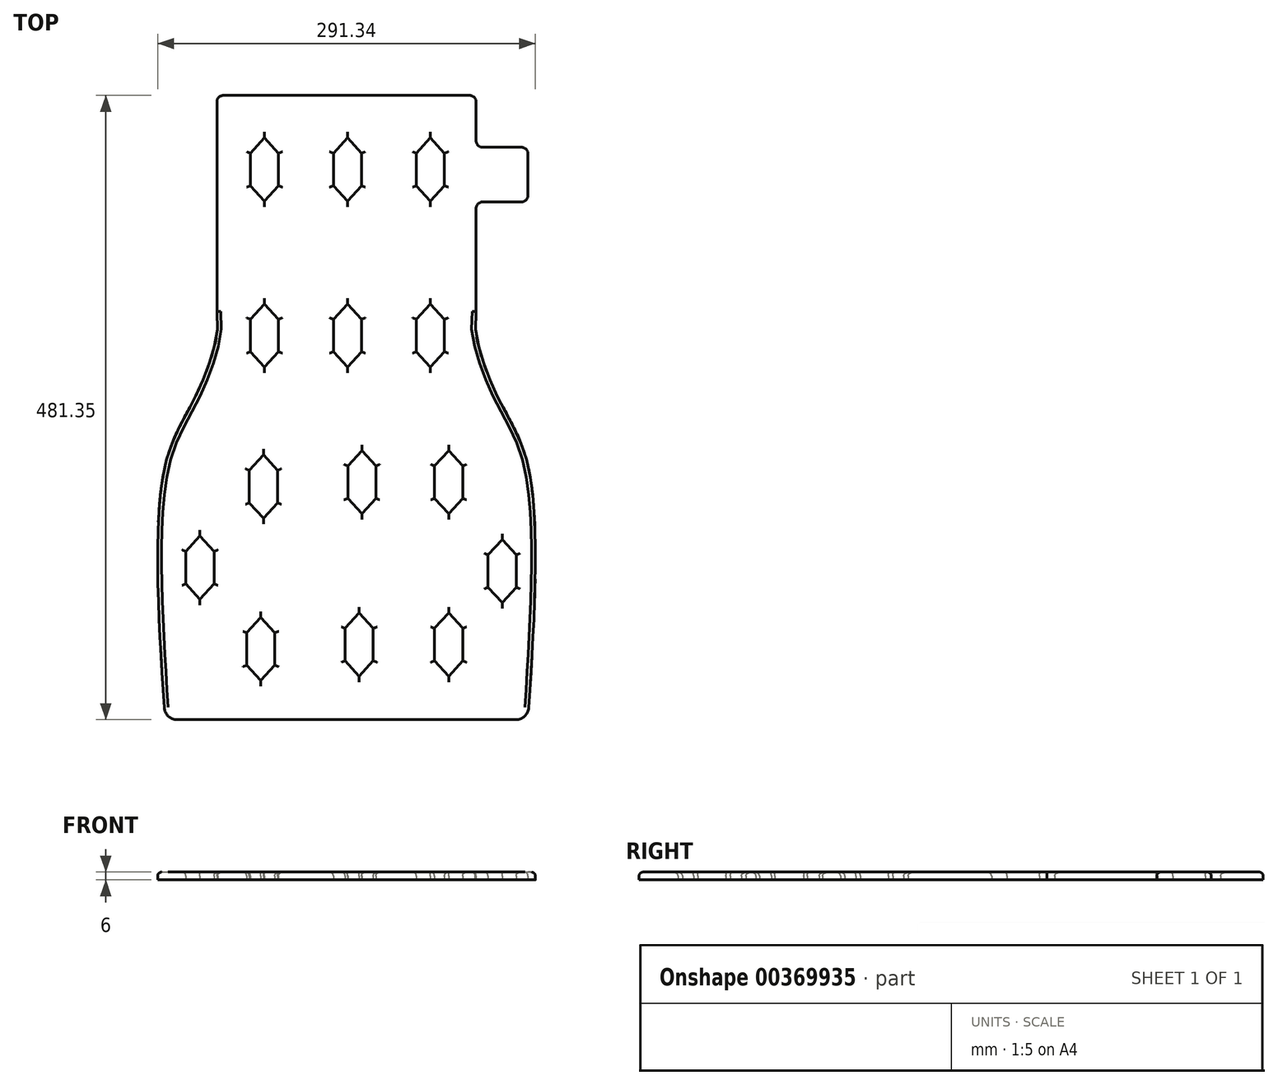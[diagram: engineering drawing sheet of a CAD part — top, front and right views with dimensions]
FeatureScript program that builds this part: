
annotation { "Feature Type Name" : "Feature", "Feature Type Description" : "" }
export const myFeature = defineFeature(function(context is Context, id is Id, definition is map)
    precondition{}
    {
        {
            var Q0;
            Q0=qCreatedBy(makeId("Top.planeOp"),FACE);
            var sketch = newSketch(context, id + "F0", { "sketchPlane" : qUnion([Q0])});
            skLineSegment(sketch, "E0", {"start": v(0, 262.18) * mm, "end": v(95, 262.18) * mm});
            skLineSegment(sketch, "E1", {"start": v(0, 262.18) * mm, "end": v(-95, 262.18) * mm});
            skLineSegment(sketch, "E2", {"start": v(130.62, -219.17) * mm, "end": v(-130.62, -219.17) * mm});
            skFitSpline(sketch, "E3", {"points": [v(-140, -219.17) * mm, v(-140, -23.78) * mm, v(-116.25, 30.48) * mm, v(-100, 77.75) * mm, v(-100, 95.38) * mm], "startDerivative": vector(-34.72, 539.25) * mm, "endDerivative": vector(-13.07, 120.29) * mm});
            skFitSpline(sketch, "E4.MirrorCS", {"points": [v(140, -219.17) * mm, v(140, -23.78) * mm, v(116.25, 30.48) * mm, v(100, 77.75) * mm, v(100, 95.38) * mm], "startDerivative": vector(34.72, 539.25) * mm, "endDerivative": vector(13.07, 120.29) * mm});
            skLineSegment(sketch, "E5", {"start": v(-100, 257.18) * mm, "end": v(-100, 95.38) * mm});
            skLineSegment(sketch, "E6", {"start": v(100, 95.38) * mm, "end": v(100, 175.09) * mm});
            skPoint(sketch, "E7.visualSharp", {"position": v(-100, 262.18) * mm});
            skArc(sketch, "E7.filletArc", {"start": v(-95, 262.18) * mm, "mid": v(-98.54, 260.72) * mm, "end": v(-100, 257.18) * mm});
            skPoint(sketch, "E8.visualSharp", {"position": v(100, 262.18) * mm});
            skArc(sketch, "E8.filletArc", {"start": v(100, 257.18) * mm, "mid": v(98.54, 260.72) * mm, "end": v(95, 262.18) * mm});
            skLineSegment(sketch, "E9", {"start": v(100, 262.18) * mm, "end": v(100, 227.18) * mm});
            skLineSegment(sketch, "E10", {"start": v(105, 222.18) * mm, "end": v(135, 222.18) * mm});
            skLineSegment(sketch, "E11", {"start": v(140, 217.18) * mm, "end": v(140, 185.09) * mm});
            skLineSegment(sketch, "E12", {"start": v(135, 180.09) * mm, "end": v(105, 180.09) * mm});
            skArc(sketch, "E13.filletArc", {"start": v(105, 180.09) * mm, "mid": v(101.46, 178.62) * mm, "end": v(100, 175.09) * mm});
            skPoint(sketch, "E14.visualSharp", {"position": v(140, 180.09) * mm});
            skArc(sketch, "E14.filletArc", {"start": v(135, 180.09) * mm, "mid": v(138.54, 181.55) * mm, "end": v(140, 185.09) * mm});
            skPoint(sketch, "E15.visualSharp", {"position": v(140, 222.18) * mm});
            skArc(sketch, "E15.filletArc", {"start": v(140, 217.18) * mm, "mid": v(138.54, 220.72) * mm, "end": v(135, 222.18) * mm});
            skPoint(sketch, "E16.visualSharp", {"position": v(100, 222.18) * mm});
            skArc(sketch, "E16.filletArc", {"start": v(100, 227.18) * mm, "mid": v(101.46, 223.65) * mm, "end": v(105, 222.18) * mm});
            skArc(sketch, "E17.filletArc", {"start": v(130.62, -219.17) * mm, "mid": v(137.46, -216.46) * mm, "end": v(140.6, -209.8) * mm});
            skArc(sketch, "E18.filletArc", {"start": v(-140.6, -209.8) * mm, "mid": v(-137.46, -216.46) * mm, "end": v(-130.62, -219.17) * mm});
            skLineSegment(sketch, "E19.left", {"start": v(-52.46, 217.58) * mm, "end": v(-52.46, 192.58) * mm});
            skLineSegment(sketch, "E19.right", {"start": v(-74.1, 217.58) * mm, "end": v(-74.1, 192.58) * mm});
            skPoint(sketch, "E20.endSnap0", {"position": v(-63.28, 136.49) * mm});
            skLineSegment(sketch, "E21", {"start": v(-63.28, 180.7) * mm, "end": v(-52.46, 192.58) * mm});
            skPoint(sketch, "E22.endSnap0", {"position": v(46.38, 56.52) * mm});
            skLineSegment(sketch, "E23.MirrorCS", {"start": v(-63.28, 229.44) * mm, "end": v(-52.46, 217.58) * mm});
            skLineSegment(sketch, "E24.MirrorCS", {"start": v(-74.1, 217.58) * mm, "end": v(-63.28, 229.44) * mm});
            skLineSegment(sketch, "E25.0.1.0", {"start": v(-74.1, 89.58) * mm, "end": v(-63.28, 101.44) * mm});
            skLineSegment(sketch, "E25.0.1.1", {"start": v(-74.1, 89.58) * mm, "end": v(-74.1, 64.58) * mm});
            skLineSegment(sketch, "E25.0.1.2", {"start": v(-74.1, 64.58) * mm, "end": v(-63.28, 52.7) * mm});
            skLineSegment(sketch, "E25.0.1.3", {"start": v(-63.28, 52.7) * mm, "end": v(-52.46, 64.58) * mm});
            skLineSegment(sketch, "E25.0.1.4", {"start": v(-52.46, 89.58) * mm, "end": v(-52.46, 64.58) * mm});
            skLineSegment(sketch, "E25.0.1.5", {"start": v(-63.28, 101.44) * mm, "end": v(-52.46, 89.58) * mm});
            skLineSegment(sketch, "E25.1.0.0", {"start": v(-10.1, 217.58) * mm, "end": v(0.72, 229.44) * mm});
            skLineSegment(sketch, "E25.1.0.1", {"start": v(-10.1, 217.58) * mm, "end": v(-10.1, 192.58) * mm});
            skLineSegment(sketch, "E25.1.0.2", {"start": v(-10.1, 192.58) * mm, "end": v(0.72, 180.7) * mm});
            skLineSegment(sketch, "E25.1.0.3", {"start": v(0.72, 180.7) * mm, "end": v(11.54, 192.58) * mm});
            skLineSegment(sketch, "E25.1.0.4", {"start": v(11.54, 217.58) * mm, "end": v(11.54, 192.58) * mm});
            skLineSegment(sketch, "E25.1.0.5", {"start": v(0.72, 229.44) * mm, "end": v(11.54, 217.58) * mm});
            skLineSegment(sketch, "E25.1.1.0", {"start": v(-10.1, 89.58) * mm, "end": v(0.72, 101.44) * mm});
            skLineSegment(sketch, "E25.1.1.1", {"start": v(-10.1, 89.58) * mm, "end": v(-10.1, 64.58) * mm});
            skLineSegment(sketch, "E25.1.1.2", {"start": v(-10.1, 64.58) * mm, "end": v(0.72, 52.7) * mm});
            skLineSegment(sketch, "E25.1.1.3", {"start": v(0.72, 52.7) * mm, "end": v(11.54, 64.58) * mm});
            skLineSegment(sketch, "E25.1.1.4", {"start": v(11.54, 89.58) * mm, "end": v(11.54, 64.58) * mm});
            skLineSegment(sketch, "E25.1.1.5", {"start": v(0.72, 101.44) * mm, "end": v(11.54, 89.58) * mm});
            skLineSegment(sketch, "E25.2.0.0", {"start": v(53.9, 217.58) * mm, "end": v(64.72, 229.44) * mm});
            skLineSegment(sketch, "E25.2.0.1", {"start": v(53.9, 217.58) * mm, "end": v(53.9, 192.58) * mm});
            skLineSegment(sketch, "E25.2.0.2", {"start": v(53.9, 192.58) * mm, "end": v(64.72, 180.7) * mm});
            skLineSegment(sketch, "E25.2.0.3", {"start": v(64.72, 180.7) * mm, "end": v(75.54, 192.58) * mm});
            skLineSegment(sketch, "E25.2.0.4", {"start": v(75.54, 217.58) * mm, "end": v(75.54, 192.58) * mm});
            skLineSegment(sketch, "E25.2.0.5", {"start": v(64.72, 229.44) * mm, "end": v(75.54, 217.58) * mm});
            skLineSegment(sketch, "E25.2.1.0", {"start": v(53.9, 89.58) * mm, "end": v(64.72, 101.44) * mm});
            skLineSegment(sketch, "E25.2.1.1", {"start": v(53.9, 89.58) * mm, "end": v(53.9, 64.58) * mm});
            skLineSegment(sketch, "E25.2.1.2", {"start": v(53.9, 64.58) * mm, "end": v(64.72, 52.7) * mm});
            skLineSegment(sketch, "E25.2.1.3", {"start": v(64.72, 52.7) * mm, "end": v(75.54, 64.58) * mm});
            skLineSegment(sketch, "E25.2.1.4", {"start": v(75.54, 89.58) * mm, "end": v(75.54, 64.58) * mm});
            skLineSegment(sketch, "E25.2.1.5", {"start": v(64.72, 101.44) * mm, "end": v(75.54, 89.58) * mm});
            skLineSegment(sketch, "E25.direction1", {"start": v(-63.28, 180.7) * mm, "end": v(0.72, 180.7) * mm, "construction": true});
            skLineSegment(sketch, "E25.direction2", {"start": v(-63.28, 180.7) * mm, "end": v(-63.28, 52.7) * mm, "construction": true});
            skLineSegment(sketch, "E26.left", {"start": v(-53.3, -26.91) * mm, "end": v(-53.3, -51.91) * mm});
            skLineSegment(sketch, "E26.right", {"start": v(-74.93, -26.91) * mm, "end": v(-74.93, -51.91) * mm});
            skLineSegment(sketch, "E27", {"start": v(-74.93, -51.91) * mm, "end": v(-64.11, -63.78) * mm});
            skLineSegment(sketch, "E28", {"start": v(-64.11, -63.78) * mm, "end": v(-53.3, -51.91) * mm});
            skLineSegment(sketch, "E29.MirrorCS", {"start": v(-64.11, -15.05) * mm, "end": v(-53.3, -26.91) * mm});
            skLineSegment(sketch, "E30.MirrorCS", {"start": v(-74.93, -26.91) * mm, "end": v(-64.11, -15.05) * mm});
            skLineSegment(sketch, "E31.0.1.0", {"start": v(-76.97, -152.13) * mm, "end": v(-66.16, -140.27) * mm});
            skLineSegment(sketch, "E31.0.1.1", {"start": v(-66.16, -140.27) * mm, "end": v(-55.34, -152.13) * mm});
            skLineSegment(sketch, "E31.0.1.2", {"start": v(-55.34, -152.13) * mm, "end": v(-55.34, -177.13) * mm});
            skLineSegment(sketch, "E31.0.1.3", {"start": v(-66.16, -189) * mm, "end": v(-55.34, -177.13) * mm});
            skLineSegment(sketch, "E31.0.1.4", {"start": v(-76.97, -177.13) * mm, "end": v(-66.16, -189) * mm});
            skLineSegment(sketch, "E31.0.1.5", {"start": v(-76.97, -152.13) * mm, "end": v(-76.97, -177.13) * mm});
            skLineSegment(sketch, "E31.1.0.0", {"start": v(1.03, -23.5) * mm, "end": v(11.84, -11.63) * mm});
            skLineSegment(sketch, "E31.1.0.1", {"start": v(11.84, -11.63) * mm, "end": v(22.66, -23.5) * mm});
            skLineSegment(sketch, "E31.1.0.2", {"start": v(22.66, -23.5) * mm, "end": v(22.66, -48.5) * mm});
            skLineSegment(sketch, "E31.1.0.3", {"start": v(11.84, -60.36) * mm, "end": v(22.66, -48.5) * mm});
            skLineSegment(sketch, "E31.1.0.4", {"start": v(1.03, -48.5) * mm, "end": v(11.84, -60.36) * mm});
            skLineSegment(sketch, "E31.1.0.5", {"start": v(1.03, -23.5) * mm, "end": v(1.03, -48.5) * mm});
            skLineSegment(sketch, "E31.1.1.0", {"start": v(-1.02, -148.72) * mm, "end": v(9.8, -136.85) * mm});
            skLineSegment(sketch, "E31.1.1.1", {"start": v(9.8, -136.85) * mm, "end": v(20.61, -148.72) * mm});
            skLineSegment(sketch, "E31.1.1.2", {"start": v(20.61, -148.72) * mm, "end": v(20.61, -173.72) * mm});
            skLineSegment(sketch, "E31.1.1.3", {"start": v(9.8, -185.58) * mm, "end": v(20.61, -173.72) * mm});
            skLineSegment(sketch, "E31.1.1.4", {"start": v(-1.02, -173.72) * mm, "end": v(9.8, -185.58) * mm});
            skLineSegment(sketch, "E31.1.1.5", {"start": v(-1.02, -148.72) * mm, "end": v(-1.02, -173.72) * mm});
            skLineSegment(sketch, "E31.direction1", {"start": v(-64.11, -63.78) * mm, "end": v(11.84, -60.36) * mm, "construction": true});
            skLineSegment(sketch, "E31.direction2", {"start": v(-64.11, -63.78) * mm, "end": v(-66.16, -189) * mm, "construction": true});
            skLineSegment(sketch, "E32.left", {"start": v(-102.2, -89.43) * mm, "end": v(-102.2, -114.43) * mm});
            skLineSegment(sketch, "E32.right", {"start": v(-123.84, -89.43) * mm, "end": v(-123.84, -114.43) * mm});
            skLineSegment(sketch, "E33", {"start": v(-123.84, -114.43) * mm, "end": v(-113.02, -126.3) * mm});
            skLineSegment(sketch, "E34", {"start": v(-113.02, -126.3) * mm, "end": v(-102.2, -114.43) * mm});
            skLineSegment(sketch, "E35.MirrorCS", {"start": v(-113.02, -77.56) * mm, "end": v(-102.2, -89.43) * mm});
            skLineSegment(sketch, "E36.MirrorCS", {"start": v(-123.84, -89.43) * mm, "end": v(-113.02, -77.56) * mm});
            skLineSegment(sketch, "E37.left", {"start": v(130.86, -92.1) * mm, "end": v(130.86, -117.1) * mm});
            skLineSegment(sketch, "E37.right", {"start": v(109.23, -92.1) * mm, "end": v(109.23, -117.1) * mm});
            skLineSegment(sketch, "E38", {"start": v(109.23, -117.1) * mm, "end": v(120.04, -128.96) * mm});
            skLineSegment(sketch, "E39", {"start": v(120.04, -128.96) * mm, "end": v(130.86, -117.1) * mm});
            skLineSegment(sketch, "E40.MirrorCS", {"start": v(120.04, -80.23) * mm, "end": v(130.86, -92.1) * mm});
            skLineSegment(sketch, "E41.MirrorCS", {"start": v(109.23, -92.1) * mm, "end": v(120.04, -80.23) * mm});
            skLineSegment(sketch, "E42.left", {"start": v(89.58, -23.5) * mm, "end": v(89.58, -48.5) * mm});
            skLineSegment(sketch, "E42.right", {"start": v(67.95, -23.5) * mm, "end": v(67.95, -48.5) * mm});
            skLineSegment(sketch, "E43", {"start": v(67.95, -48.5) * mm, "end": v(78.76, -60.36) * mm});
            skLineSegment(sketch, "E44", {"start": v(78.76, -60.36) * mm, "end": v(89.58, -48.5) * mm});
            skLineSegment(sketch, "E45.MirrorCS", {"start": v(78.76, -11.63) * mm, "end": v(89.58, -23.5) * mm});
            skLineSegment(sketch, "E46.MirrorCS", {"start": v(67.95, -23.5) * mm, "end": v(78.76, -11.63) * mm});
            skLineSegment(sketch, "E47.left", {"start": v(89.58, -148.72) * mm, "end": v(89.58, -173.72) * mm});
            skLineSegment(sketch, "E47.right", {"start": v(67.95, -148.72) * mm, "end": v(67.95, -173.72) * mm});
            skLineSegment(sketch, "E48", {"start": v(67.95, -173.72) * mm, "end": v(78.76, -185.58) * mm});
            skLineSegment(sketch, "E49", {"start": v(78.76, -185.58) * mm, "end": v(89.58, -173.72) * mm});
            skLineSegment(sketch, "E50.MirrorCS", {"start": v(78.76, -136.85) * mm, "end": v(89.58, -148.72) * mm});
            skLineSegment(sketch, "E51.MirrorCS", {"start": v(67.95, -148.72) * mm, "end": v(78.76, -136.85) * mm});
            skLineSegment(sketch, "E52", {"start": v(-74.1, 192.58) * mm, "end": v(-63.28, 180.7) * mm});
            skSolve(sketch);
        }
        {
            var Q0;
            Q0=makeQuery(id+"F0.imprint","IMPRINT",FACE,{"disambiguationData":[TD([[makeQuery(id+"F0.imprint","IMPRINT",EDGE,{"derivedFrom":sQuery(id+"F0.wireOp",EDGE,"E0")}),-1.0]])]});
            extrude(context, id + "F1", {"entities" : qUnion([Q0]), "depth" : 6 * mm, "offsetDistance" : 25 * mm});
        }
        {
            var Q0;
            Q0=makeQuery(id+"F1.opExtrude","CAP_FACE",FACE,{"disambiguationData":[OSD([sQuery(id+"F0.wireOp",EDGE,"E0"),sQuery(id+"F0.wireOp",EDGE,"E1"),sQuery(id+"F0.wireOp",EDGE,"E2"),sQuery(id+"F0.wireOp",EDGE,"E3"),sQuery(id+"F0.wireOp",EDGE,"E4.MirrorCS"),sQuery(id+"F0.wireOp",EDGE,"E5"),sQuery(id+"F0.wireOp",EDGE,"E6"),sQuery(id+"F0.wireOp",EDGE,"E7.filletArc"),sQuery(id+"F0.wireOp",EDGE,"E8.filletArc"),sQuery(id+"F0.wireOp",EDGE,"E9"),sQuery(id+"F0.wireOp",EDGE,"E10"),sQuery(id+"F0.wireOp",EDGE,"E11"),sQuery(id+"F0.wireOp",EDGE,"E12"),sQuery(id+"F0.wireOp",EDGE,"E13.filletArc"),sQuery(id+"F0.wireOp",EDGE,"E14.filletArc"),sQuery(id+"F0.wireOp",EDGE,"E15.filletArc"),sQuery(id+"F0.wireOp",EDGE,"E16.filletArc"),sQuery(id+"F0.wireOp",EDGE,"E17.filletArc"),sQuery(id+"F0.wireOp",EDGE,"E18.filletArc"),sQuery(id+"F0.wireOp",EDGE,"E19.left"),sQuery(id+"F0.wireOp",EDGE,"E19.right"),sQuery(id+"F0.wireOp",EDGE,"E21"),sQuery(id+"F0.wireOp",EDGE,"E23.MirrorCS"),sQuery(id+"F0.wireOp",EDGE,"E24.MirrorCS"),sQuery(id+"F0.wireOp",EDGE,"E25.0.1.0"),sQuery(id+"F0.wireOp",EDGE,"E25.0.1.1"),sQuery(id+"F0.wireOp",EDGE,"E25.0.1.2"),sQuery(id+"F0.wireOp",EDGE,"E25.0.1.3"),sQuery(id+"F0.wireOp",EDGE,"E25.0.1.4"),sQuery(id+"F0.wireOp",EDGE,"E25.0.1.5"),sQuery(id+"F0.wireOp",EDGE,"E25.1.0.0"),sQuery(id+"F0.wireOp",EDGE,"E25.1.0.1"),sQuery(id+"F0.wireOp",EDGE,"E25.1.0.2"),sQuery(id+"F0.wireOp",EDGE,"E25.1.0.3"),sQuery(id+"F0.wireOp",EDGE,"E25.1.0.4"),sQuery(id+"F0.wireOp",EDGE,"E25.1.0.5"),sQuery(id+"F0.wireOp",EDGE,"E25.1.1.0"),sQuery(id+"F0.wireOp",EDGE,"E25.1.1.1"),sQuery(id+"F0.wireOp",EDGE,"E25.1.1.2"),sQuery(id+"F0.wireOp",EDGE,"E25.1.1.3"),sQuery(id+"F0.wireOp",EDGE,"E25.1.1.4"),sQuery(id+"F0.wireOp",EDGE,"E25.1.1.5"),sQuery(id+"F0.wireOp",EDGE,"E25.2.0.0"),sQuery(id+"F0.wireOp",EDGE,"E25.2.0.1"),sQuery(id+"F0.wireOp",EDGE,"E25.2.0.2"),sQuery(id+"F0.wireOp",EDGE,"E25.2.0.3"),sQuery(id+"F0.wireOp",EDGE,"E25.2.0.4"),sQuery(id+"F0.wireOp",EDGE,"E25.2.0.5"),sQuery(id+"F0.wireOp",EDGE,"E25.2.1.0"),sQuery(id+"F0.wireOp",EDGE,"E25.2.1.1"),sQuery(id+"F0.wireOp",EDGE,"E25.2.1.2"),sQuery(id+"F0.wireOp",EDGE,"E25.2.1.3"),sQuery(id+"F0.wireOp",EDGE,"E25.2.1.4"),sQuery(id+"F0.wireOp",EDGE,"E25.2.1.5"),sQuery(id+"F0.wireOp",EDGE,"E26.left"),sQuery(id+"F0.wireOp",EDGE,"E26.right"),sQuery(id+"F0.wireOp",EDGE,"E27"),sQuery(id+"F0.wireOp",EDGE,"E28"),sQuery(id+"F0.wireOp",EDGE,"E29.MirrorCS"),sQuery(id+"F0.wireOp",EDGE,"E30.MirrorCS"),sQuery(id+"F0.wireOp",EDGE,"E31.0.1.0"),sQuery(id+"F0.wireOp",EDGE,"E31.0.1.1"),sQuery(id+"F0.wireOp",EDGE,"E31.0.1.2"),sQuery(id+"F0.wireOp",EDGE,"E31.0.1.3"),sQuery(id+"F0.wireOp",EDGE,"E31.0.1.4"),sQuery(id+"F0.wireOp",EDGE,"E31.0.1.5"),sQuery(id+"F0.wireOp",EDGE,"E31.1.0.0"),sQuery(id+"F0.wireOp",EDGE,"E31.1.0.1"),sQuery(id+"F0.wireOp",EDGE,"E31.1.0.2"),sQuery(id+"F0.wireOp",EDGE,"E31.1.0.3"),sQuery(id+"F0.wireOp",EDGE,"E31.1.0.4"),sQuery(id+"F0.wireOp",EDGE,"E31.1.0.5"),sQuery(id+"F0.wireOp",EDGE,"E31.1.1.0"),sQuery(id+"F0.wireOp",EDGE,"E31.1.1.1"),sQuery(id+"F0.wireOp",EDGE,"E31.1.1.2"),sQuery(id+"F0.wireOp",EDGE,"E31.1.1.3"),sQuery(id+"F0.wireOp",EDGE,"E31.1.1.4"),sQuery(id+"F0.wireOp",EDGE,"E31.1.1.5"),sQuery(id+"F0.wireOp",EDGE,"E32.left"),sQuery(id+"F0.wireOp",EDGE,"E32.right"),sQuery(id+"F0.wireOp",EDGE,"E33"),sQuery(id+"F0.wireOp",EDGE,"E34"),sQuery(id+"F0.wireOp",EDGE,"E35.MirrorCS"),sQuery(id+"F0.wireOp",EDGE,"E36.MirrorCS"),sQuery(id+"F0.wireOp",EDGE,"E37.left"),sQuery(id+"F0.wireOp",EDGE,"E37.right"),sQuery(id+"F0.wireOp",EDGE,"E38"),sQuery(id+"F0.wireOp",EDGE,"E39"),sQuery(id+"F0.wireOp",EDGE,"E40.MirrorCS"),sQuery(id+"F0.wireOp",EDGE,"E41.MirrorCS"),sQuery(id+"F0.wireOp",EDGE,"E42.left"),sQuery(id+"F0.wireOp",EDGE,"E42.right"),sQuery(id+"F0.wireOp",EDGE,"E43"),sQuery(id+"F0.wireOp",EDGE,"E44"),sQuery(id+"F0.wireOp",EDGE,"E45.MirrorCS"),sQuery(id+"F0.wireOp",EDGE,"E46.MirrorCS"),sQuery(id+"F0.wireOp",EDGE,"E47.left"),sQuery(id+"F0.wireOp",EDGE,"E47.right"),sQuery(id+"F0.wireOp",EDGE,"E48"),sQuery(id+"F0.wireOp",EDGE,"E49"),sQuery(id+"F0.wireOp",EDGE,"E50.MirrorCS"),sQuery(id+"F0.wireOp",EDGE,"E51.MirrorCS"),sQuery(id+"F0.wireOp",EDGE,"E52")])],"isStart":false});
            fillet(context, id + "F2", {"entities" : qUnion([Q0]), "radius" : 3 * mm, "tangentPropagation" : true, "allowEdgeOverflow" : false});
        }
    });
